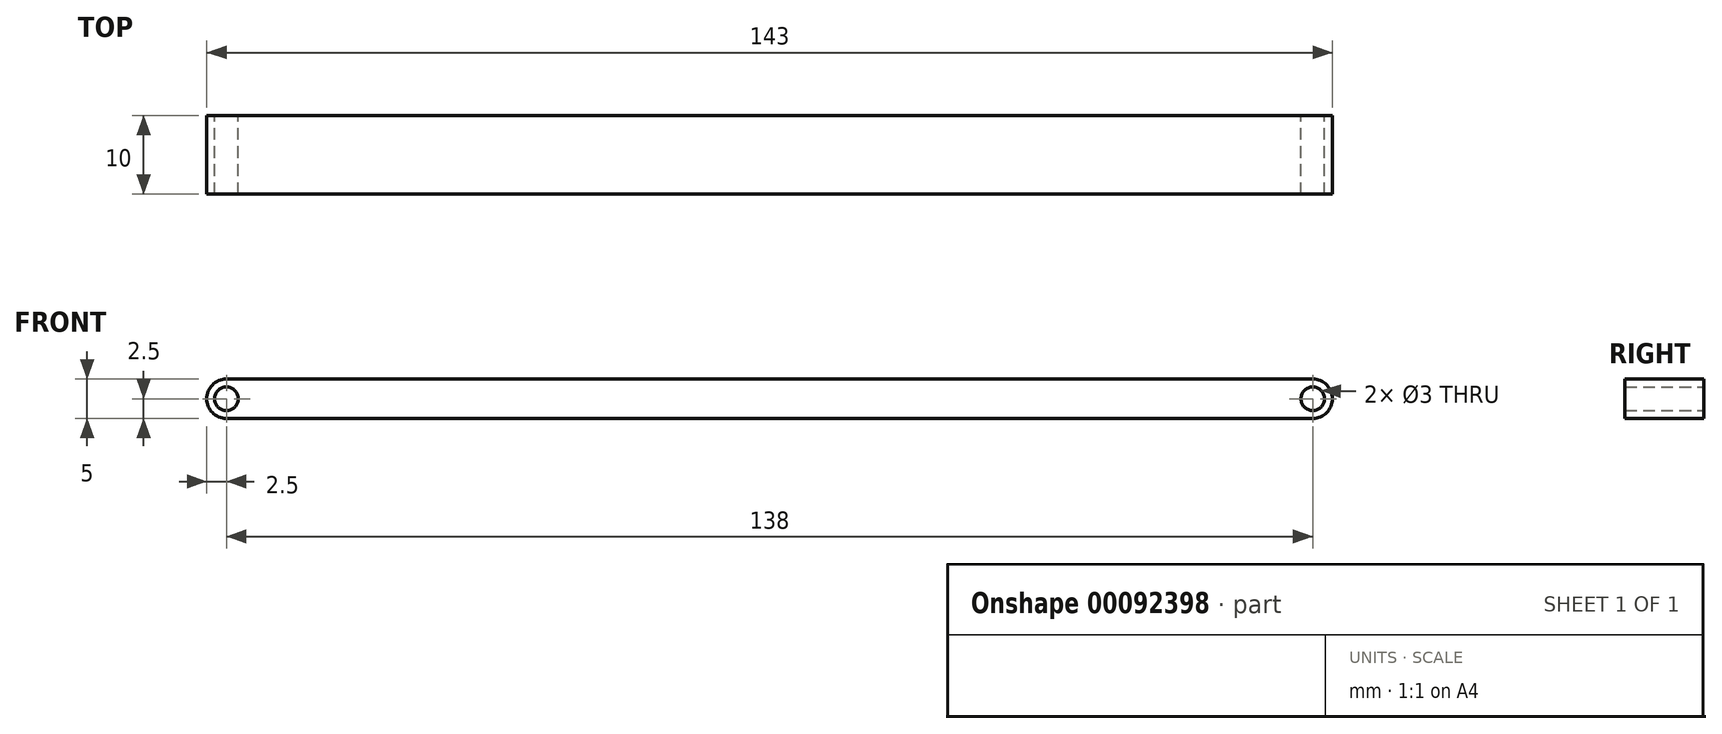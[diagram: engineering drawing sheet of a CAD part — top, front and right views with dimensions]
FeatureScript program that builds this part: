
annotation { "Feature Type Name" : "Feature", "Feature Type Description" : "" }
export const myFeature = defineFeature(function(context is Context, id is Id, definition is map)
    precondition{}
    {
        {
            var Q0;
            Q0=qCreatedBy(makeId("Front.planeOp"),FACE);
            var sketch = newSketch(context, id + "F0", { "sketchPlane" : qUnion([Q0])});
            skCircle(sketch, "E0", {"center": v(0, 0) * mm, "radius": 1.5 * mm});
            skCircle(sketch, "E1", {"center": v(-138, 0) * mm, "radius": 1.5 * mm});
            skArc(sketch, "E2", {"start": v(-138, 2.5) * mm, "mid": v(-140.5, 0) * mm, "end": v(-138, -2.5) * mm});
            skArc(sketch, "E3", {"start": v(0, -2.5) * mm, "mid": v(2.5, 0) * mm, "end": v(0, 2.5) * mm});
            skLineSegment(sketch, "E4", {"start": v(-138, 2.5) * mm, "end": v(0, 2.5) * mm});
            skLineSegment(sketch, "E5", {"start": v(-138, -2.5) * mm, "end": v(0, -2.5) * mm});
            skSolve(sketch);
        }
        {
            var Q0;
            Q0=makeQuery(id+"F0.imprint","IMPRINT",FACE,{"disambiguationData":[TD([[makeQuery(id+"F0.imprint","IMPRINT",EDGE,{"derivedFrom":sQuery(id+"F0.wireOp",EDGE,"E0")}),-1.0]])]});
            extrude(context, id + "F1", {"entities" : qUnion([Q0]), "endBound" : BoundingType.SYMMETRIC, "depth" : 10 * mm});
        }
    });
